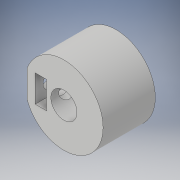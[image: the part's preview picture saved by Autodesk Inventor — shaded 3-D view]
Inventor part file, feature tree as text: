
AUTODESK INVENTOR PART (.ipt)
format: ipt  version: 2019 (Build 230136000, 136)  size: 136,704 bytes
history: native  units: mm
features: sketch x5, extrude x4, plane x1
ambient origin geometry x8: Origin, YZ Plane, XZ Plane, XY Plane, X Axis, Y Axis, Z Axis, Center Point
bodies: Solid1 (feature_tree)
feature tree (10):
  extrude  "Extrusion1"  Depth=5.0mm
  plane  "Work Plane1"
  extrude  "Extrusion2"  Depth=10.0mm
  extrude  "Extrusion3"  Depth=2.2mm
  extrude  "Extrusion4"  Depth=7.0mm TaperAngle=0.0deg
  sketch  "Sketch6"  dims[d12=3.0mm d13=7.0mm d14=8.0mm d15=0.0mm d16=6.0mm d17=10.0mm d18=0.5mm d19=8.0mm d20=0.0mm]
  sketch  "Sketch1"  dims[d0=15.0mm d1=5.0mm]
  sketch  "Sketch2"  dims[d2=10.0mm d3=0.0mm d4=3.0mm]
  sketch  "Sketch4"  dims[d5=5.5mm d6=2.2mm]
  sketch  "Sketch5"  dims[d7=5.2mm d8=7.0mm d9=0.0mm]
